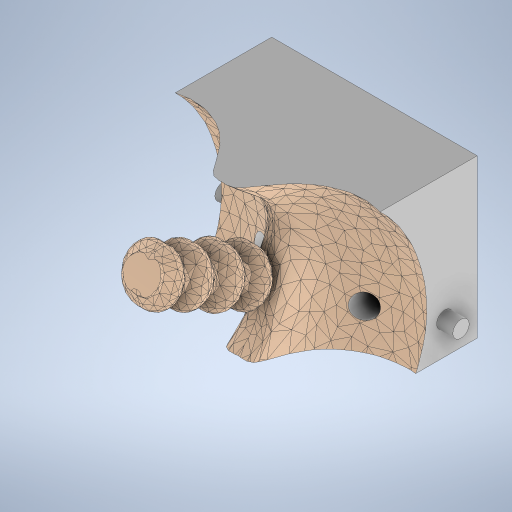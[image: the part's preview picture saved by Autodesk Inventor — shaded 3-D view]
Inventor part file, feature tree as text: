
AUTODESK INVENTOR PART (.ipt)
format: ipt  version: 2024 (Build 280153000, 153)  size: 11,512,832 bytes
history: native  units: mm
features: other x6, sketch x6, extrude x5, plane x2, chamfer x1
ambient origin geometry x8: Origin, YZ Plane, XZ Plane, XY Plane, X Axis, Y Axis, Z Axis, Center Point
bodies: Body1 (feature_tree)
feature tree (20):
  other  "M.ipt"
  plane  "Plano de trabajo1"
  extrude  "Extrusión1"  [1 undecoded]
  other  "Combinar1"
  sketch  "Boceto3"  dims[d2=550.0mm d3=520.0mm]
  sketch  "Boceto4"  dims[d4=550.0mm d5=0.0mm d6=129.8482mm]
  plane  "Plano de trabajo2"
  sketch  "Boceto5"  dims[d17=180.0mm d18=180.0mm]
  extrude  "Extrusión2"  Depth=520.0mm
  extrude  "Extrusión3"  Depth=129.8482mm
  extrude  "Extrusión4"  Depth=180.0mm
  extrude  "Extrusión5"  Depth=180.0mm
  chamfer  "Chaflán1"  Distance=180.0mm
  other  "Sólido1::M.ipt"
  other  "OperaciónIdentificador1"
  sketch  "Boceto1"  dims[d0=25.0mm d1=-365.0mm]
  other  "Sólido2"
  sketch  "Boceto6"  dims[d22=326.0mm d23=180.0mm]
  sketch  "Boceto7"  dims[d24=180.0mm d25=180.0mm d26=10.0mm d27=0.0mm d28=1000.0mm d29=0.0mm d30=30.0mm d31=30.0mm d32=15.0mm d33=15.0mm d34=205.0mm d35=0.0mm d36=0.0mm d40=20.0mm d41=20.0mm d42=80.0mm d43=0.0mm d44=5.0mm d45=2.0mm d46=45.0deg d14=0.5mm d15=0.872665mm d16=0.5mm d19=0.5mm d20=0.872665mm d21=0.5mm d47=0.15mm d48=0.25mm d49=0.375mm d50=14.3117mm d51=0.75mm d52=20.594885mm d53=0.0625mm d54=0.75mm d55=0.375mm]
  other  "Sólido1"
note: 1 required parameter value undecoded (feature->parameter linkage not recoverable at this tier; creation-order binding heuristic only, values carry confidence <= 0.55)
